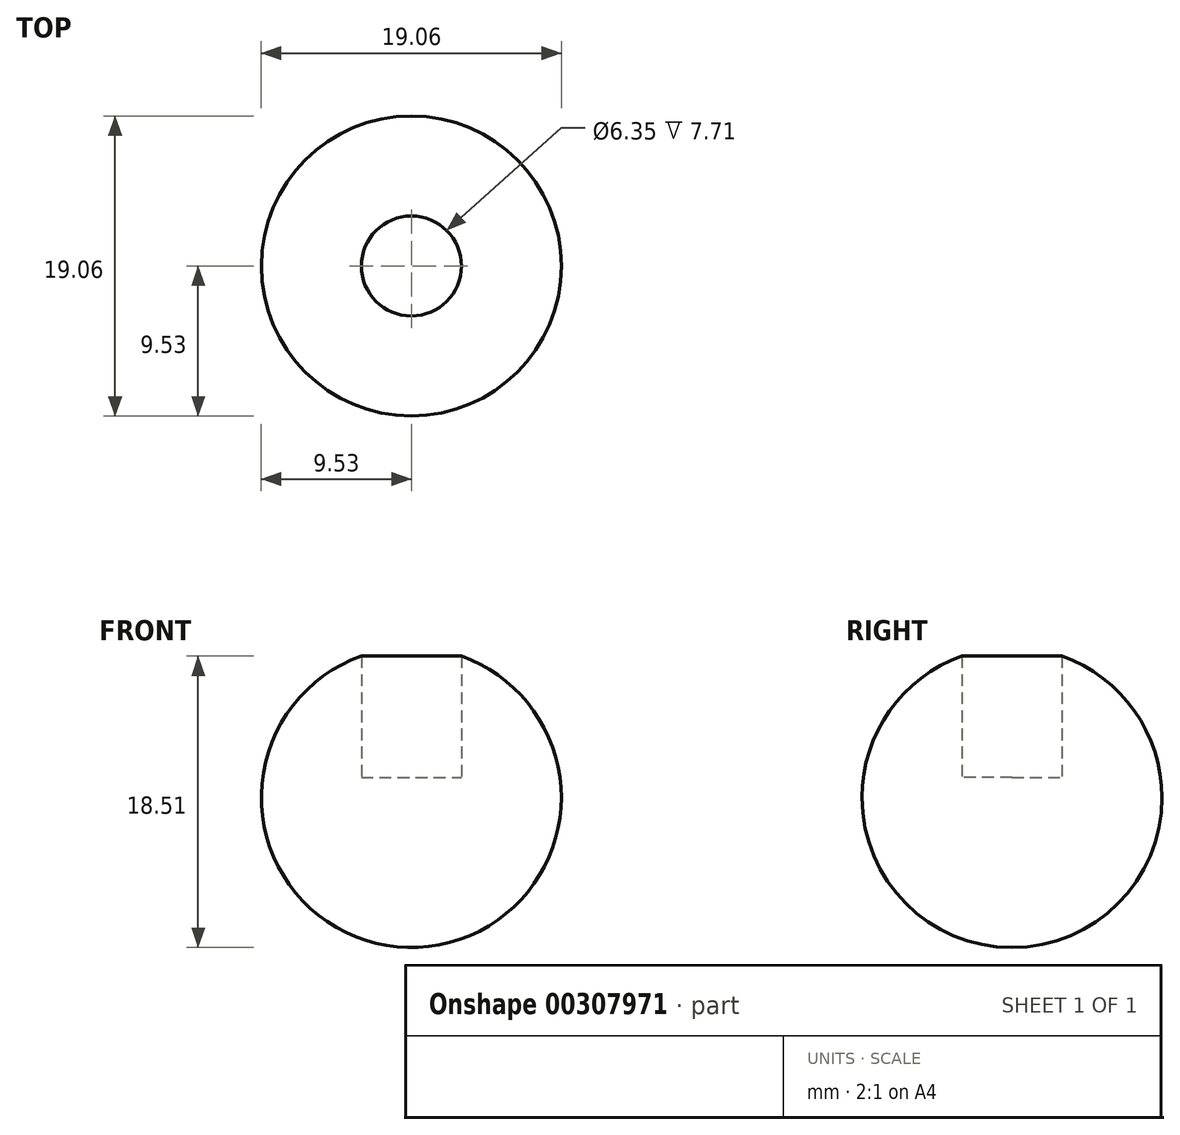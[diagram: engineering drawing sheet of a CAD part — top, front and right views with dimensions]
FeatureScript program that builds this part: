
annotation { "Feature Type Name" : "Feature", "Feature Type Description" : "" }
export const myFeature = defineFeature(function(context is Context, id is Id, definition is map)
    precondition{}
    {
        {
            var Q0;
            Q0=qCreatedBy(makeId("Front.planeOp"),FACE);
            var sketch = newSketch(context, id + "F0", { "sketchPlane" : qUnion([Q0])});
            skCircle(sketch, "E0", {"center": v(0, 0) * mm, "radius": 9.52 * mm});
            skSolve(sketch);
        }
        {
            var Q0;
            Q0=qCreatedBy(makeId("Top.planeOp"),FACE);
            var sketch = newSketch(context, id + "F1", { "sketchPlane" : qUnion([Q0])});
            skArc(sketch, "E1", {"start": v(0, 9.53) * mm, "mid": v(-9.53, 0) * mm, "end": v(0, -9.53) * mm});
            skLineSegment(sketch, "E2", {"start": v(0, 9.53) * mm, "end": v(0, -9.53) * mm});
            skSolve(sketch);
        }
        {
            var Q0;
            Q0=makeQuery(id+"F1.imprint","IMPRINT",FACE,{"disambiguationData":[TD([[makeQuery(id+"F1.imprint","IMPRINT",EDGE,{"derivedFrom":sQuery(id+"F1.wireOp",EDGE,"E1")}),1.0]])]});
            var Q1;
            Q1=sQuery(id+"F0.wireOp",EDGE,"E0");
            revolve(context, id + "F2", {"entities" : qUnion([Q0]), "axis" : qUnion([Q1]), "revolveType" : RevolveType.FULL});
        }
        {
            var Q0;
            Q0=qCreatedBy(makeId("Top.planeOp"),FACE);
            cPlane(context, id + "F3", {"entities" : qUnion([Q0]), "cplaneType" : CPlaneType.OFFSET, "offset" : 1.27 * mm, "width" : 152.4 * mm, "height" : 152.4 * mm});
        }
        {
            var Q0;
            Q0=qCreatedBy(id+"F3.planeOp",FACE);
            var sketch = newSketch(context, id + "F4", { "sketchPlane" : qUnion([Q0])});
            skCircle(sketch, "E3", {"center": v(0, 0) * mm, "radius": 3.18 * mm});
            skSolve(sketch);
        }
        {
            var Q0;
            Q0 = qSketchRegion(id + "F4", true);
            extrude(context, id + "F5", {"entities" : qUnion([Q0]), "operationType" : NewBodyOperationType.REMOVE, "depth" : 50.8 * mm});
        }
    });
